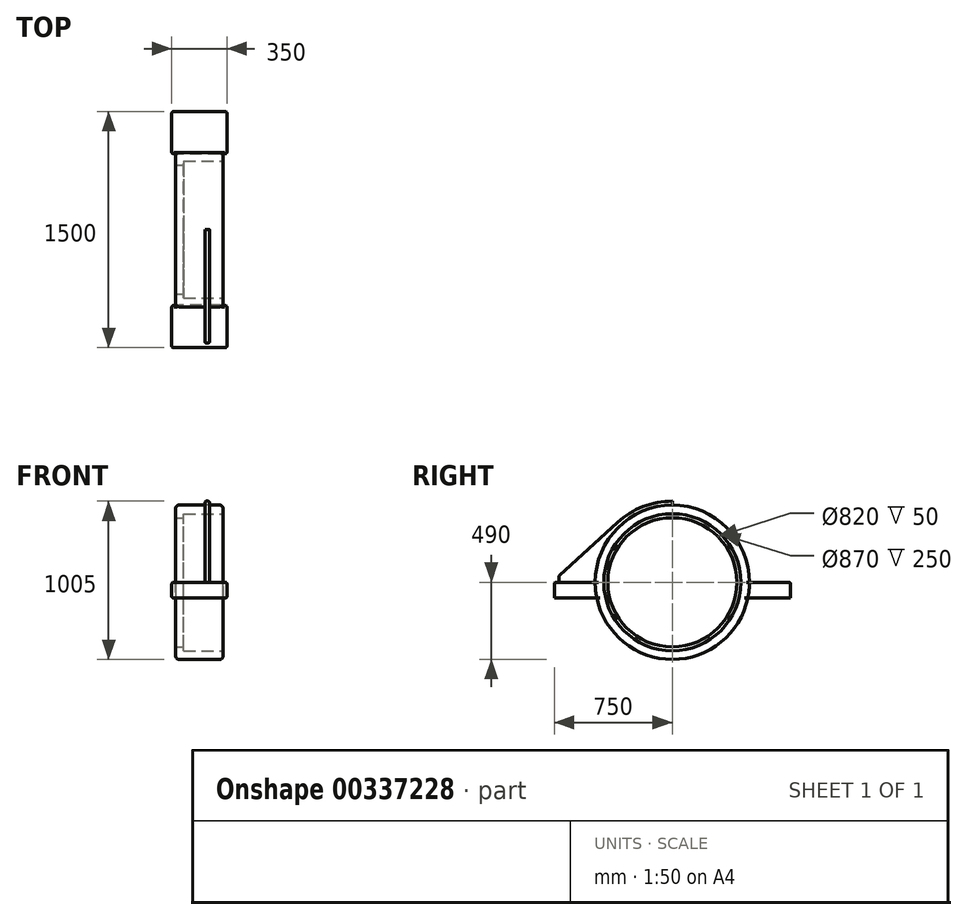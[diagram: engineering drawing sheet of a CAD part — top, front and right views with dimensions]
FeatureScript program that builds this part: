
annotation { "Feature Type Name" : "Feature", "Feature Type Description" : "" }
export const myFeature = defineFeature(function(context is Context, id is Id, definition is map)
    precondition{}
    {
        {
            var Q0;
            Q0=qCreatedBy(makeId("Front.planeOp"),FACE);
            var sketch = newSketch(context, id + "F0", { "sketchPlane" : qUnion([Q0])});
            skLineSegment(sketch, "E0", {"start": v(150, 435) * mm, "end": v(150, 490) * mm});
            skLineSegment(sketch, "E1", {"start": v(150, 490) * mm, "end": v(-150, 490) * mm});
            skLineSegment(sketch, "E2", {"start": v(-150, 490) * mm, "end": v(-150, 410) * mm});
            skLineSegment(sketch, "E3", {"start": v(0, 490) * mm, "end": v(0, 0) * mm, "construction": true});
            skLineSegment(sketch, "E4", {"start": v(0, 0) * mm, "end": v(-175, 0) * mm, "construction": true});
            skLineSegment(sketch, "E5", {"start": v(-100, 435) * mm, "end": v(-100, 410) * mm});
            skLineSegment(sketch, "E6", {"start": v(-100, 410) * mm, "end": v(-150, 410) * mm});
            skLineSegment(sketch, "E7", {"start": v(-100, 435) * mm, "end": v(150, 435) * mm});
            skSolve(sketch);
        }
        {
            var Q0;
            Q0=qSketchRegion(id+"F0",true);
            var Q1;
            Q1=sQuery(id+"F0.wireOp",EDGE,"E4");
            revolve(context, id + "F1", {"entities" : qUnion([Q0]), "axis" : qUnion([Q1]), "revolveType" : RevolveType.FULL});
        }
        {
            var Q0;
            Q0=qCreatedBy(makeId("Right.planeOp"),FACE);
            var sketch = newSketch(context, id + "F2", { "sketchPlane" : qUnion([Q0])});
            skLineSegment(sketch, "E8.bottom", {"start": v(-750, 0) * mm, "end": v(750, 0) * mm});
            skLineSegment(sketch, "E8.top", {"start": v(-750, -100) * mm, "end": v(750, -100) * mm});
            skLineSegment(sketch, "E8.left", {"start": v(-750, 0) * mm, "end": v(-750, -100) * mm});
            skLineSegment(sketch, "E8.right", {"start": v(750, 0) * mm, "end": v(750, -100) * mm});
            skLineSegment(sketch, "E9", {"start": v(-750, -50) * mm, "end": v(750, -50) * mm, "construction": true});
            skLineSegment(sketch, "E10", {"start": v(0, 0) * mm, "end": v(0, -50) * mm});
            skCircle(sketch, "E11.0", {"center": v(0, 0) * mm, "radius": 490 * mm});
            skSolve(sketch);
        }
        {
            var Q0;
            {var subQ0=sQuery(id+"F2.wireOp",EDGE,"E8.left");Q0=makeQuery(id+"F2.imprint","IMPRINT",FACE,{"disambiguationData":[TD([[makeQuery(id+"F2.imprint","IMPRINT",EDGE,{"derivedFrom":subQ0}),1.0]])]});}
            var Q1;
            {var subQ0=sQuery(id+"F2.wireOp",EDGE,"E8.right");Q1=makeQuery(id+"F2.imprint","IMPRINT",FACE,{"disambiguationData":[TD([[makeQuery(id+"F2.imprint","IMPRINT",EDGE,{"derivedFrom":subQ0}),-1.0]])]});}
            extrude(context, id + "F3", {"entities" : qUnion([Q0, Q1]), "operationType" : NewBodyOperationType.ADD, "depth" : 350 * mm, "symmetric" : true});
        }
        {
            var Q0;
            Q0=qCreatedBy(makeId("Right.planeOp"),FACE);
            cPlane(context, id + "F4", {"entities" : qUnion([Q0]), "cplaneType" : CPlaneType.OFFSET, "offset" : 50 * mm, "width" : 150 * mm, "height" : 150 * mm});
        }
        {
            var Q0;
            Q0=qCreatedBy(id+"F4.planeOp",FACE);
            var sketch = newSketch(context, id + "F5", { "sketchPlane" : qUnion([Q0])});
            skLineSegment(sketch, "E12", {"start": v(0, 0) * mm, "end": v(0, 515) * mm});
            skLineSegment(sketch, "E13", {"start": v(-720, 0) * mm, "end": v(-720, 40) * mm});
            skLineSegment(sketch, "E14", {"start": v(-720, 40) * mm, "end": v(-347.24, 380.33) * mm});
            skArc(sketch, "E15", {"start": v(0, 515) * mm, "mid": v(-186.22, 480.15) * mm, "end": v(-347.24, 380.33) * mm});
            skLineSegment(sketch, "E16.0", {"start": v(-720, 0) * mm, "end": v(-490, 0) * mm});
            skPoint(sketch, "E17.orphan", {"position": v(-750, 0) * mm});
            skLineSegment(sketch, "E18", {"start": v(-490, 0) * mm, "end": v(0, 0) * mm});
            skArc(sketch, "E19.0", {"start": v(0, 490) * mm, "mid": v(-346.48, 346.48) * mm, "end": v(-490, 0) * mm});
            skPoint(sketch, "E20.orphan", {"position": v(490, 0) * mm});
            skSolve(sketch);
        }
        {
            var Q0;
            Q0=makeQuery(id+"F5.imprint","IMPRINT",FACE,{"disambiguationData":[TD([[makeQuery(id+"F5.imprint","IMPRINT",EDGE,{"derivedFrom":sQuery(id+"F5.wireOp",EDGE,"E13")}),-1.0]])]});
            extrude(context, id + "F6", {"entities" : qUnion([Q0]), "operationType" : NewBodyOperationType.ADD, "depth" : 30 * mm, "symmetric" : true});
        }
        {
            var Q0;
            Q0=makeQuery(id+"F6.opExtrude","CAP_EDGE",EDGE,{"disambiguationData":[OSD([sQuery(id+"F5.wireOp",EDGE,"E16.0")])],"isStart":false});
            var Q1;
            Q1=makeQuery(id+"F6.opExtrude","SWEPT_EDGE",EDGE,{"disambiguationData":[OSD([sQuery(id+"F5.wireOp",EDGE,"E13"),sQuery(id+"F5.wireOp",EDGE,"E16.0")])]});
            var Q2;
            Q2=makeQuery(id+"F6.opExtrude","CAP_EDGE",EDGE,{"disambiguationData":[OSD([sQuery(id+"F5.wireOp",EDGE,"E13")])],"isStart":false});
            var Q3;
            Q3=makeQuery(id+"F6.opExtrude","CAP_EDGE",EDGE,{"disambiguationData":[OSD([sQuery(id+"F5.wireOp",EDGE,"E14")])],"isStart":false});
            var Q4;
            Q4=makeQuery(id+"F6.opExtrude","SWEPT_EDGE",EDGE,{"disambiguationData":[OSD([sQuery(id+"F5.wireOp",EDGE,"E13"),sQuery(id+"F5.wireOp",EDGE,"E14")])]});
            var Q5;
            Q5=makeQuery(id+"F6.opExtrude","CAP_EDGE",EDGE,{"disambiguationData":[OSD([sQuery(id+"F5.wireOp",EDGE,"E14")])],"isStart":true});
            var Q6;
            Q6=makeQuery(id+"F6.opExtrude","CAP_EDGE",EDGE,{"disambiguationData":[OSD([sQuery(id+"F5.wireOp",EDGE,"E13")])],"isStart":true});
            var Q7;
            {var subQ0=sQuery(id+"F5.wireOp",EDGE,"E19.0");Q7=makeQuery(id+"F4xZpk5MUKX7Juj_1.1.F6.boolean.opBoolean","MERGE",EDGE,{"derivedFrom":[makeQuery(id+"F6.opExtrude","CAP_EDGE",EDGE,{"disambiguationData":[OSD([subQ0])],"isStart":true}),makeQuery(id+"F4xZpk5MUKX7Juj_1.1.F6.opExtrude","CAP_EDGE",EDGE,{"disambiguationData":[OSD([subQ0])],"isStart":true})]});}
            var Q8;
            {var subQ0=makeQuery(id+"F1.opRevolve","SWEPT_FACE",FACE,{"disambiguationData":[OSD([sQuery(id+"F0.wireOp",EDGE,"E1")])]});var subQ1=sQuery(id+"F5.wireOp",EDGE,"E19.0");var subQ2=sQuery(id+"F5.wireOp",EDGE,"E16.0");var subQ3=sQuery(id+"F5.wireOp",EDGE,"E15");var subQ4=sQuery(id+"F5.wireOp",EDGE,"E14");var subQ5=sQuery(id+"F5.wireOp",EDGE,"E13");var subQ6=sQuery(id+"F5.wireOp",EDGE,"E12");var subQ7=sQuery(id+"F2.wireOp",EDGE,"E8.bottom");var subQ8=sQuery(id+"F2.wireOp",EDGE,"E11.0");var subQ9=makeQuery(id+"F2.imprint","INTERSECT",VERTEX,{"disambiguationData":[OD(0.0)],"derivedFrom":[subQ7,subQ8]});var subQ10=makeQuery(id+"F3.opExtrude","SWEPT_FACE",FACE,{"disambiguationData":[OSD([subQ7]),TDD([makeQuery(id+"F2.imprint","IMPRINT",EDGE,{"disambiguationData":[TD([[makeQuery(id+"F2.imprint","INTERSECT",VERTEX,{"derivedFrom":[subQ7,sQuery(id+"F2.wireOp",EDGE,"E8.left")]}),-1.0]])],"derivedFrom":subQ7})])]});var subQ11=makeQuery(id+"F6.opExtrude","CAP_FACE",FACE,{"disambiguationData":[OSD([subQ6,subQ5,subQ4,subQ3,subQ2,subQ1])],"isStart":true});Q8=makeQuery(id+"FQAO3xyy8PO0jJj_1.1.F6.boolean.opBoolean","SPLIT",EDGE,{"disambiguationData":[TD([subQ11])],"derivedFrom":makeQuery(id+"F6.boolean.opBoolean","SPLIT",EDGE,{"disambiguationData":[TD([makeQuery(id+"F1.opRevolve","SWEPT_FACE",FACE,{"disambiguationData":[OSD([sQuery(id+"F0.wireOp",EDGE,"E2")])]})])],"derivedFrom":makeQuery(id+"F3.boolean.opBoolean","SPLIT",EDGE,{"disambiguationData":[topologyDisambiguationEdgeConnected([subQ0,subQ10])],"derivedFrom":makeQuery(id+"F3.opExtrude","SWEPT_EDGE",EDGE,{"disambiguationData":[OSD([subQ7,subQ8]),TDD([subQ9])]})})})});}
            var Q9;
            {var subQ0=sQuery(id+"F5.wireOp",EDGE,"E19.0");Q9=makeQuery(id+"F4xZpk5MUKX7Juj_1.1.FQAO3xyy8PO0jJj_1.1.F6.boolean.opBoolean","MERGE",EDGE,{"derivedFrom":[makeQuery(id+"FQAO3xyy8PO0jJj_1.1.F6.opExtrude","CAP_EDGE",EDGE,{"disambiguationData":[OSD([subQ0])],"isStart":true}),makeQuery(id+"F4xZpk5MUKX7Juj_1.1.FQAO3xyy8PO0jJj_1.1.F6.opExtrude","CAP_EDGE",EDGE,{"disambiguationData":[OSD([subQ0])],"isStart":true})]});}
            var Q10;
            Q10=makeQuery(id+"FQAO3xyy8PO0jJj_1.1.F6.opExtrude","CAP_EDGE",EDGE,{"disambiguationData":[OSD([sQuery(id+"F5.wireOp",EDGE,"E16.0")])],"isStart":true});
            var Q11;
            Q11=makeQuery(id+"FQAO3xyy8PO0jJj_1.1.F6.opExtrude","CAP_EDGE",EDGE,{"disambiguationData":[OSD([sQuery(id+"F5.wireOp",EDGE,"E14")])],"isStart":true});
            var Q12;
            Q12=makeQuery(id+"FQAO3xyy8PO0jJj_1.1.F6.opExtrude","CAP_EDGE",EDGE,{"disambiguationData":[OSD([sQuery(id+"F5.wireOp",EDGE,"E14")])],"isStart":false});
            var Q13;
            {var subQ0=sQuery(id+"F5.wireOp",EDGE,"E19.0");Q13=makeQuery(id+"F4xZpk5MUKX7Juj_1.1.F6.boolean.opBoolean","MERGE",EDGE,{"derivedFrom":[makeQuery(id+"F6.opExtrude","CAP_EDGE",EDGE,{"disambiguationData":[OSD([subQ0])],"isStart":false}),makeQuery(id+"F4xZpk5MUKX7Juj_1.1.F6.opExtrude","CAP_EDGE",EDGE,{"disambiguationData":[OSD([subQ0])],"isStart":false})]});}
            var Q14;
            {var subQ0=sQuery(id+"F5.wireOp",EDGE,"E19.0");Q14=makeQuery(id+"F4xZpk5MUKX7Juj_1.1.FQAO3xyy8PO0jJj_1.1.F6.boolean.opBoolean","MERGE",EDGE,{"derivedFrom":[makeQuery(id+"FQAO3xyy8PO0jJj_1.1.F6.opExtrude","CAP_EDGE",EDGE,{"disambiguationData":[OSD([subQ0])],"isStart":false}),makeQuery(id+"F4xZpk5MUKX7Juj_1.1.FQAO3xyy8PO0jJj_1.1.F6.opExtrude","CAP_EDGE",EDGE,{"disambiguationData":[OSD([subQ0])],"isStart":false})]});}
            var Q15;
            {var subQ0=sQuery(id+"F2.wireOp",EDGE,"E11.0");var subQ1=sQuery(id+"F2.wireOp",EDGE,"E8.bottom");var subQ2=makeQuery(id+"F2.imprint","INTERSECT",VERTEX,{"disambiguationData":[OD(0.0)],"derivedFrom":[subQ1,subQ0]});var subQ4=makeQuery(id+"F3.opExtrude","SWEPT_FACE",FACE,{"disambiguationData":[OSD([subQ1]),TDD([makeQuery(id+"F2.imprint","IMPRINT",EDGE,{"disambiguationData":[TD([[makeQuery(id+"F2.imprint","INTERSECT",VERTEX,{"derivedFrom":[subQ1,sQuery(id+"F2.wireOp",EDGE,"E8.left")]}),-1.0]])],"derivedFrom":subQ1})])]});var subQ5=makeQuery(id+"F1.opRevolve","SWEPT_FACE",FACE,{"disambiguationData":[OSD([sQuery(id+"F0.wireOp",EDGE,"E1")])]});var subQ6=makeQuery(id+"F1.opRevolve","SWEPT_FACE",FACE,{"disambiguationData":[OSD([sQuery(id+"F0.wireOp",EDGE,"E2")])]});Q15=makeQuery(id+"FQAO3xyy8PO0jJj_1.1.F6.boolean.opBoolean","SPLIT",EDGE,{"disambiguationData":[TD([subQ6])],"derivedFrom":makeQuery(id+"F6.boolean.opBoolean","SPLIT",EDGE,{"disambiguationData":[TD([subQ6])],"derivedFrom":makeQuery(id+"F3.boolean.opBoolean","SPLIT",EDGE,{"disambiguationData":[topologyDisambiguationEdgeConnected([subQ5,subQ4])],"derivedFrom":makeQuery(id+"F3.opExtrude","SWEPT_EDGE",EDGE,{"disambiguationData":[OSD([subQ1,subQ0]),TDD([subQ2])]})})})});}
            var Q16;
            Q16=makeQuery(id+"FQAO3xyy8PO0jJj_1.1.F6.opExtrude","CAP_EDGE",EDGE,{"disambiguationData":[OSD([sQuery(id+"F5.wireOp",EDGE,"E16.0")])],"isStart":false});
            var Q17;
            Q17=makeQuery(id+"FQAO3xyy8PO0jJj_1.1.F6.opExtrude","SWEPT_EDGE",EDGE,{"disambiguationData":[OSD([sQuery(id+"F5.wireOp",EDGE,"E13"),sQuery(id+"F5.wireOp",EDGE,"E16.0")])]});
            var Q18;
            {var subQ0=sQuery(id+"F2.wireOp",EDGE,"E11.0");var subQ1=sQuery(id+"F2.wireOp",EDGE,"E8.bottom");var subQ2=makeQuery(id+"F2.imprint","INTERSECT",VERTEX,{"disambiguationData":[OD(0.0)],"derivedFrom":[subQ1,subQ0]});var subQ3=makeQuery(id+"F3.opExtrude","SWEPT_FACE",FACE,{"disambiguationData":[OSD([subQ1]),TDD([makeQuery(id+"F2.imprint","IMPRINT",EDGE,{"disambiguationData":[TD([[makeQuery(id+"F2.imprint","INTERSECT",VERTEX,{"derivedFrom":[subQ1,sQuery(id+"F2.wireOp",EDGE,"E8.left")]}),-1.0]])],"derivedFrom":subQ1})])]});var subQ4=makeQuery(id+"F1.opRevolve","SWEPT_FACE",FACE,{"disambiguationData":[OSD([sQuery(id+"F0.wireOp",EDGE,"E1")])]});Q18=makeQuery(id+"F6.boolean.opBoolean","SPLIT",EDGE,{"disambiguationData":[TD([makeQuery(id+"F1.opRevolve","SWEPT_FACE",FACE,{"disambiguationData":[OSD([sQuery(id+"F0.wireOp",EDGE,"E0")])]})])],"derivedFrom":makeQuery(id+"F3.boolean.opBoolean","SPLIT",EDGE,{"disambiguationData":[topologyDisambiguationEdgeConnected([subQ4,subQ3])],"derivedFrom":makeQuery(id+"F3.opExtrude","SWEPT_EDGE",EDGE,{"disambiguationData":[OSD([subQ1,subQ0]),TDD([subQ2])]})})});}
            var Q19;
            Q19=makeQuery(id+"F4xZpk5MUKX7Juj_1.1.FQAO3xyy8PO0jJj_1.1.F6.opExtrude","SWEPT_EDGE",EDGE,{"disambiguationData":[OSD([sQuery(id+"F5.wireOp",EDGE,"E13"),sQuery(id+"F5.wireOp",EDGE,"E14")])]});
            var Q20;
            Q20=makeQuery(id+"F4xZpk5MUKX7Juj_1.1.F6.opExtrude","SWEPT_EDGE",EDGE,{"disambiguationData":[OSD([sQuery(id+"F5.wireOp",EDGE,"E13"),sQuery(id+"F5.wireOp",EDGE,"E14")])]});
            var Q21;
            Q21=makeQuery(id+"F4xZpk5MUKX7Juj_1.1.F6.opExtrude","CAP_EDGE",EDGE,{"disambiguationData":[OSD([sQuery(id+"F5.wireOp",EDGE,"E13")])],"isStart":true});
            var Q22;
            Q22=makeQuery(id+"F4xZpk5MUKX7Juj_1.1.F6.opExtrude","CAP_EDGE",EDGE,{"disambiguationData":[OSD([sQuery(id+"F5.wireOp",EDGE,"E13")])],"isStart":false});
            var Q23;
            Q23=makeQuery(id+"F4xZpk5MUKX7Juj_1.1.F6.opExtrude","SWEPT_EDGE",EDGE,{"disambiguationData":[OSD([sQuery(id+"F5.wireOp",EDGE,"E13"),sQuery(id+"F5.wireOp",EDGE,"E16.0")])]});
            var Q24;
            Q24=makeQuery(id+"F4xZpk5MUKX7Juj_1.1.FQAO3xyy8PO0jJj_1.1.F6.opExtrude","SWEPT_EDGE",EDGE,{"disambiguationData":[OSD([sQuery(id+"F5.wireOp",EDGE,"E13"),sQuery(id+"F5.wireOp",EDGE,"E16.0")])]});
            var Q25;
            Q25=makeQuery(id+"F4xZpk5MUKX7Juj_1.1.FQAO3xyy8PO0jJj_1.1.F6.opExtrude","CAP_EDGE",EDGE,{"disambiguationData":[OSD([sQuery(id+"F5.wireOp",EDGE,"E13")])],"isStart":false});
            var Q26;
            {var subQ0=sQuery(id+"F5.wireOp",EDGE,"E19.0");var subQ1=sQuery(id+"F5.wireOp",EDGE,"E16.0");var subQ2=sQuery(id+"F5.wireOp",EDGE,"E15");var subQ3=sQuery(id+"F5.wireOp",EDGE,"E14");var subQ4=sQuery(id+"F5.wireOp",EDGE,"E13");var subQ5=sQuery(id+"F5.wireOp",EDGE,"E12");var subQ6=makeQuery(id+"F6.opExtrude","CAP_FACE",FACE,{"disambiguationData":[OSD([subQ5,subQ4,subQ3,subQ2,subQ1,subQ0])],"isStart":true});var subQ7=sQuery(id+"F2.wireOp",EDGE,"E8.bottom");var subQ8=sQuery(id+"F2.wireOp",EDGE,"E11.0");var subQ9=makeQuery(id+"F2.imprint","INTERSECT",VERTEX,{"disambiguationData":[OD(1.0)],"derivedFrom":[subQ7,subQ8]});var subQ10=makeQuery(id+"F3.opExtrude","SWEPT_FACE",FACE,{"disambiguationData":[OSD([subQ7]),TDD([makeQuery(id+"F2.imprint","IMPRINT",EDGE,{"disambiguationData":[TD([[makeQuery(id+"F2.imprint","INTERSECT",VERTEX,{"derivedFrom":[subQ7,sQuery(id+"F2.wireOp",EDGE,"E8.right")]}),1.0]])],"derivedFrom":subQ7})])]});var subQ11=makeQuery(id+"F1.opRevolve","SWEPT_FACE",FACE,{"disambiguationData":[OSD([sQuery(id+"F0.wireOp",EDGE,"E1")])]});Q26=makeQuery(id+"F4xZpk5MUKX7Juj_1.1.FQAO3xyy8PO0jJj_1.1.F6.boolean.opBoolean","SPLIT",EDGE,{"disambiguationData":[TD([subQ6])],"derivedFrom":makeQuery(id+"F4xZpk5MUKX7Juj_1.1.F6.boolean.opBoolean","SPLIT",EDGE,{"disambiguationData":[TD([makeQuery(id+"F1.opRevolve","SWEPT_FACE",FACE,{"disambiguationData":[OSD([sQuery(id+"F0.wireOp",EDGE,"E2")])]})])],"derivedFrom":makeQuery(id+"F3.boolean.opBoolean","SPLIT",EDGE,{"disambiguationData":[topologyDisambiguationEdgeConnected([subQ11,subQ10])],"derivedFrom":makeQuery(id+"F3.opExtrude","SWEPT_EDGE",EDGE,{"disambiguationData":[OSD([subQ7,subQ8]),TDD([subQ9])]})})})});}
            var Q27;
            {var subQ0=sQuery(id+"F2.wireOp",EDGE,"E11.0");var subQ1=sQuery(id+"F2.wireOp",EDGE,"E8.bottom");var subQ2=makeQuery(id+"F2.imprint","INTERSECT",VERTEX,{"disambiguationData":[OD(1.0)],"derivedFrom":[subQ1,subQ0]});var subQ4=makeQuery(id+"F1.opRevolve","SWEPT_FACE",FACE,{"disambiguationData":[OSD([sQuery(id+"F0.wireOp",EDGE,"E1")])]});var subQ5=makeQuery(id+"F1.opRevolve","SWEPT_FACE",FACE,{"disambiguationData":[OSD([sQuery(id+"F0.wireOp",EDGE,"E2")])]});var subQ6=makeQuery(id+"F3.opExtrude","SWEPT_FACE",FACE,{"disambiguationData":[OSD([subQ1]),TDD([makeQuery(id+"F2.imprint","IMPRINT",EDGE,{"disambiguationData":[TD([[makeQuery(id+"F2.imprint","INTERSECT",VERTEX,{"derivedFrom":[subQ1,sQuery(id+"F2.wireOp",EDGE,"E8.right")]}),1.0]])],"derivedFrom":subQ1})])]});Q27=makeQuery(id+"F4xZpk5MUKX7Juj_1.1.FQAO3xyy8PO0jJj_1.1.F6.boolean.opBoolean","SPLIT",EDGE,{"disambiguationData":[TD([subQ5])],"derivedFrom":makeQuery(id+"F4xZpk5MUKX7Juj_1.1.F6.boolean.opBoolean","SPLIT",EDGE,{"disambiguationData":[TD([subQ5])],"derivedFrom":makeQuery(id+"F3.boolean.opBoolean","SPLIT",EDGE,{"disambiguationData":[topologyDisambiguationEdgeConnected([subQ4,subQ6])],"derivedFrom":makeQuery(id+"F3.opExtrude","SWEPT_EDGE",EDGE,{"disambiguationData":[OSD([subQ1,subQ0]),TDD([subQ2])]})})})});}
            var Q28;
            {var subQ0=sQuery(id+"F2.wireOp",EDGE,"E11.0");var subQ1=sQuery(id+"F2.wireOp",EDGE,"E8.bottom");var subQ2=makeQuery(id+"F2.imprint","INTERSECT",VERTEX,{"disambiguationData":[OD(1.0)],"derivedFrom":[subQ1,subQ0]});var subQ3=makeQuery(id+"F1.opRevolve","SWEPT_FACE",FACE,{"disambiguationData":[OSD([sQuery(id+"F0.wireOp",EDGE,"E1")])]});var subQ10=makeQuery(id+"F3.opExtrude","SWEPT_FACE",FACE,{"disambiguationData":[OSD([subQ1]),TDD([makeQuery(id+"F2.imprint","IMPRINT",EDGE,{"disambiguationData":[TD([[makeQuery(id+"F2.imprint","INTERSECT",VERTEX,{"derivedFrom":[subQ1,sQuery(id+"F2.wireOp",EDGE,"E8.right")]}),1.0]])],"derivedFrom":subQ1})])]});Q28=makeQuery(id+"F4xZpk5MUKX7Juj_1.1.F6.boolean.opBoolean","SPLIT",EDGE,{"disambiguationData":[TD([makeQuery(id+"F1.opRevolve","SWEPT_FACE",FACE,{"disambiguationData":[OSD([sQuery(id+"F0.wireOp",EDGE,"E0")])]})])],"derivedFrom":makeQuery(id+"F3.boolean.opBoolean","SPLIT",EDGE,{"disambiguationData":[topologyDisambiguationEdgeConnected([subQ3,subQ10])],"derivedFrom":makeQuery(id+"F3.opExtrude","SWEPT_EDGE",EDGE,{"disambiguationData":[OSD([subQ1,subQ0]),TDD([subQ2])]})})});}
            var Q29;
            {var subQ0=sQuery(id+"F2.wireOp",EDGE,"E8.top");var subQ1=sQuery(id+"F2.wireOp",EDGE,"E11.0");var subQ2=makeQuery(id+"F2.imprint","INTERSECT",VERTEX,{"disambiguationData":[OD(1.0)],"derivedFrom":[subQ0,subQ1]});Q29=makeQuery(id+"F3.boolean.opBoolean","SPLIT",EDGE,{"disambiguationData":[topologyDisambiguationEdgeConnected([makeQuery(id+"F1.opRevolve","SWEPT_FACE",FACE,{"disambiguationData":[OSD([sQuery(id+"F0.wireOp",EDGE,"E1")])]}),makeQuery(id+"F3.opExtrude","SWEPT_FACE",FACE,{"disambiguationData":[OSD([subQ0]),TDD([makeQuery(id+"F2.imprint","IMPRINT",EDGE,{"disambiguationData":[TD([[makeQuery(id+"F2.imprint","INTERSECT",VERTEX,{"derivedFrom":[subQ0,sQuery(id+"F2.wireOp",EDGE,"E8.right")]}),1.0]])],"derivedFrom":subQ0})])]})])],"derivedFrom":makeQuery(id+"F3.opExtrude","SWEPT_EDGE",EDGE,{"disambiguationData":[OSD([subQ0,subQ1]),TDD([subQ2])]})});}
            var Q30;
            {var subQ0=sQuery(id+"F2.wireOp",EDGE,"E8.top");var subQ1=sQuery(id+"F2.wireOp",EDGE,"E11.0");var subQ2=makeQuery(id+"F2.imprint","INTERSECT",VERTEX,{"disambiguationData":[OD(0.0)],"derivedFrom":[subQ0,subQ1]});Q30=makeQuery(id+"F3.boolean.opBoolean","SPLIT",EDGE,{"disambiguationData":[topologyDisambiguationEdgeConnected([makeQuery(id+"F1.opRevolve","SWEPT_FACE",FACE,{"disambiguationData":[OSD([sQuery(id+"F0.wireOp",EDGE,"E1")])]}),makeQuery(id+"F3.opExtrude","SWEPT_FACE",FACE,{"disambiguationData":[OSD([subQ0]),TDD([makeQuery(id+"F2.imprint","IMPRINT",EDGE,{"disambiguationData":[TD([[makeQuery(id+"F2.imprint","INTERSECT",VERTEX,{"derivedFrom":[subQ0,sQuery(id+"F2.wireOp",EDGE,"E8.left")]}),-1.0]])],"derivedFrom":subQ0})])]})])],"derivedFrom":makeQuery(id+"F3.opExtrude","SWEPT_EDGE",EDGE,{"disambiguationData":[OSD([subQ0,subQ1]),TDD([subQ2])]})});}
            var Q31;
            Q31=makeQuery(id+"FQAO3xyy8PO0jJj_1.1.F6.opExtrude","CAP_EDGE",EDGE,{"disambiguationData":[OSD([sQuery(id+"F5.wireOp",EDGE,"E13")])],"isStart":true});
            var Q32;
            Q32=makeQuery(id+"FQAO3xyy8PO0jJj_1.1.F6.opExtrude","CAP_EDGE",EDGE,{"disambiguationData":[OSD([sQuery(id+"F5.wireOp",EDGE,"E13")])],"isStart":false});
            var Q33;
            Q33=makeQuery(id+"F4xZpk5MUKX7Juj_1.1.FQAO3xyy8PO0jJj_1.1.F6.opExtrude","CAP_EDGE",EDGE,{"disambiguationData":[OSD([sQuery(id+"F5.wireOp",EDGE,"E13")])],"isStart":true});
            fillet(context, id + "F7", {"entities" : qUnion([Q0, Q1, Q2, Q3, Q4, Q5, Q6, Q7, Q8, Q9, Q10, Q11, Q12, Q13, Q14, Q15, Q16, Q17, Q18, Q19, Q20, Q21, Q22, Q23, Q24, Q25, Q26, Q27, Q28, Q29, Q30, Q31, Q32, Q33]), "radius" : 10 * mm, "tangentPropagation" : true, "allowEdgeOverflow" : false});
        }
        {
            var Q0;
            {var subQ0=sQuery(id+"F0.wireOp",EDGE,"E2");var subQ1=sQuery(id+"F2.wireOp",EDGE,"E11.0");Q0=makeQuery(id+"F3.boolean.opBoolean","SPLIT",EDGE,{"disambiguationData":[topologyDisambiguationEdgeConnected([makeQuery(id+"F1.opRevolve","SWEPT_FACE",FACE,{"disambiguationData":[OSD([subQ0])]}),makeQuery(id+"F3.opExtrude","SWEPT_FACE",FACE,{"disambiguationData":[OSD([subQ1]),TDD([makeQuery(id+"F2.imprint","IMPRINT",EDGE,{"disambiguationData":[TD([[makeQuery(id+"F2.imprint","INTERSECT",VERTEX,{"disambiguationData":[OD(1.0)],"derivedFrom":[sQuery(id+"F2.wireOp",EDGE,"E8.bottom"),subQ1]}),1.0]])],"derivedFrom":subQ1})])]})])],"derivedFrom":makeQuery(id+"F1.opRevolve","SWEPT_EDGE",EDGE,{"disambiguationData":[OSD([sQuery(id+"F0.wireOp",EDGE,"E1"),subQ0])]})});}
            var Q1;
            {var subQ0=sQuery(id+"F0.wireOp",EDGE,"E2");var subQ1=sQuery(id+"F2.wireOp",EDGE,"E11.0");Q1=makeQuery(id+"F3.boolean.opBoolean","SPLIT",EDGE,{"disambiguationData":[topologyDisambiguationEdgeConnected([makeQuery(id+"F1.opRevolve","SWEPT_FACE",FACE,{"disambiguationData":[OSD([subQ0])]}),makeQuery(id+"F3.opExtrude","SWEPT_FACE",FACE,{"disambiguationData":[OSD([subQ1]),TDD([makeQuery(id+"F2.imprint","IMPRINT",EDGE,{"disambiguationData":[TD([[makeQuery(id+"F2.imprint","INTERSECT",VERTEX,{"disambiguationData":[OD(0.0)],"derivedFrom":[sQuery(id+"F2.wireOp",EDGE,"E8.bottom"),subQ1]}),-1.0]])],"derivedFrom":subQ1})])]})])],"derivedFrom":makeQuery(id+"F1.opRevolve","SWEPT_EDGE",EDGE,{"disambiguationData":[OSD([sQuery(id+"F0.wireOp",EDGE,"E1"),subQ0])]})});}
            var Q2;
            {var subQ0=sQuery(id+"F0.wireOp",EDGE,"E0");var subQ1=sQuery(id+"F2.wireOp",EDGE,"E11.0");Q2=makeQuery(id+"F3.boolean.opBoolean","SPLIT",EDGE,{"disambiguationData":[topologyDisambiguationEdgeConnected([makeQuery(id+"F1.opRevolve","SWEPT_FACE",FACE,{"disambiguationData":[OSD([subQ0])]}),makeQuery(id+"F3.opExtrude","SWEPT_FACE",FACE,{"disambiguationData":[OSD([subQ1]),TDD([makeQuery(id+"F2.imprint","IMPRINT",EDGE,{"disambiguationData":[TD([[makeQuery(id+"F2.imprint","INTERSECT",VERTEX,{"disambiguationData":[OD(0.0)],"derivedFrom":[sQuery(id+"F2.wireOp",EDGE,"E8.bottom"),subQ1]}),-1.0]])],"derivedFrom":subQ1})])]})])],"derivedFrom":makeQuery(id+"F1.opRevolve","SWEPT_EDGE",EDGE,{"disambiguationData":[OSD([subQ0,sQuery(id+"F0.wireOp",EDGE,"E1")])]})});}
            var Q3;
            {var subQ0=sQuery(id+"F0.wireOp",EDGE,"E0");var subQ1=sQuery(id+"F2.wireOp",EDGE,"E11.0");Q3=makeQuery(id+"F3.boolean.opBoolean","SPLIT",EDGE,{"disambiguationData":[topologyDisambiguationEdgeConnected([makeQuery(id+"F1.opRevolve","SWEPT_FACE",FACE,{"disambiguationData":[OSD([subQ0])]}),makeQuery(id+"F3.opExtrude","SWEPT_FACE",FACE,{"disambiguationData":[OSD([subQ1]),TDD([makeQuery(id+"F2.imprint","IMPRINT",EDGE,{"disambiguationData":[TD([[makeQuery(id+"F2.imprint","INTERSECT",VERTEX,{"disambiguationData":[OD(1.0)],"derivedFrom":[sQuery(id+"F2.wireOp",EDGE,"E8.bottom"),subQ1]}),1.0]])],"derivedFrom":subQ1})])]})])],"derivedFrom":makeQuery(id+"F1.opRevolve","SWEPT_EDGE",EDGE,{"disambiguationData":[OSD([subQ0,sQuery(id+"F0.wireOp",EDGE,"E1")])]})});}
            fillet(context, id + "F8", {"entities" : qUnion([Q0, Q1, Q2, Q3]), "radius" : 20 * mm, "tangentPropagation" : true, "allowEdgeOverflow" : false});
        }
        {
            var Q0;
            {var subQ0=sQuery(id+"F2.wireOp",EDGE,"E8.bottom");Q0=makeQuery(id+"F3.opExtrude","CAP_EDGE",EDGE,{"disambiguationData":[OSD([subQ0]),TDD([makeQuery(id+"F2.imprint","IMPRINT",EDGE,{"disambiguationData":[TD([[makeQuery(id+"F2.imprint","INTERSECT",VERTEX,{"derivedFrom":[subQ0,sQuery(id+"F2.wireOp",EDGE,"E8.right")]}),1.0]])],"derivedFrom":subQ0})])],"isStart":false});}
            var Q1;
            Q1=makeQuery(id+"F3.opExtrude","CAP_EDGE",EDGE,{"disambiguationData":[OSD([sQuery(id+"F2.wireOp",EDGE,"E8.right")])],"isStart":false});
            var Q2;
            {var subQ0=sQuery(id+"F2.wireOp",EDGE,"E11.0");Q2=makeQuery(id+"F3.opExtrude","CAP_EDGE",EDGE,{"disambiguationData":[OSD([subQ0]),TDD([makeQuery(id+"F2.imprint","IMPRINT",EDGE,{"disambiguationData":[TD([[makeQuery(id+"F2.imprint","INTERSECT",VERTEX,{"disambiguationData":[OD(1.0)],"derivedFrom":[sQuery(id+"F2.wireOp",EDGE,"E8.bottom"),subQ0]}),1.0]])],"derivedFrom":subQ0})])],"isStart":false});}
            var Q3;
            Q3=makeQuery(id+"F3.opExtrude","SWEPT_EDGE",EDGE,{"disambiguationData":[OSD([sQuery(id+"F2.wireOp",EDGE,"E8.bottom"),sQuery(id+"F2.wireOp",EDGE,"E8.right")])]});
            var Q4;
            Q4=makeQuery(id+"F3.opExtrude","CAP_EDGE",EDGE,{"disambiguationData":[OSD([sQuery(id+"F2.wireOp",EDGE,"E8.right")])],"isStart":true});
            var Q5;
            {var subQ0=sQuery(id+"F2.wireOp",EDGE,"E8.bottom");Q5=makeQuery(id+"F3.opExtrude","CAP_EDGE",EDGE,{"disambiguationData":[OSD([subQ0]),TDD([makeQuery(id+"F2.imprint","IMPRINT",EDGE,{"disambiguationData":[TD([[makeQuery(id+"F2.imprint","INTERSECT",VERTEX,{"derivedFrom":[subQ0,sQuery(id+"F2.wireOp",EDGE,"E8.right")]}),1.0]])],"derivedFrom":subQ0})])],"isStart":true});}
            var Q6;
            {var subQ0=sQuery(id+"F2.wireOp",EDGE,"E11.0");Q6=makeQuery(id+"F3.opExtrude","CAP_EDGE",EDGE,{"disambiguationData":[OSD([subQ0]),TDD([makeQuery(id+"F2.imprint","IMPRINT",EDGE,{"disambiguationData":[TD([[makeQuery(id+"F2.imprint","INTERSECT",VERTEX,{"disambiguationData":[OD(1.0)],"derivedFrom":[sQuery(id+"F2.wireOp",EDGE,"E8.bottom"),subQ0]}),1.0]])],"derivedFrom":subQ0})])],"isStart":true});}
            var Q7;
            {var subQ0=sQuery(id+"F2.wireOp",EDGE,"E11.0");Q7=makeQuery(id+"F3.opExtrude","CAP_EDGE",EDGE,{"disambiguationData":[OSD([subQ0]),TDD([makeQuery(id+"F2.imprint","IMPRINT",EDGE,{"disambiguationData":[TD([[makeQuery(id+"F2.imprint","INTERSECT",VERTEX,{"disambiguationData":[OD(0.0)],"derivedFrom":[sQuery(id+"F2.wireOp",EDGE,"E8.bottom"),subQ0]}),-1.0]])],"derivedFrom":subQ0})])],"isStart":true});}
            var Q8;
            {var subQ0=sQuery(id+"F2.wireOp",EDGE,"E8.bottom");Q8=makeQuery(id+"F3.opExtrude","CAP_EDGE",EDGE,{"disambiguationData":[OSD([subQ0]),TDD([makeQuery(id+"F2.imprint","IMPRINT",EDGE,{"disambiguationData":[TD([[makeQuery(id+"F2.imprint","INTERSECT",VERTEX,{"derivedFrom":[subQ0,sQuery(id+"F2.wireOp",EDGE,"E8.left")]}),-1.0]])],"derivedFrom":subQ0})])],"isStart":true});}
            var Q9;
            Q9=makeQuery(id+"F3.opExtrude","CAP_EDGE",EDGE,{"disambiguationData":[OSD([sQuery(id+"F2.wireOp",EDGE,"E8.left")])],"isStart":true});
            var Q10;
            Q10=makeQuery(id+"F3.opExtrude","SWEPT_EDGE",EDGE,{"disambiguationData":[OSD([sQuery(id+"F2.wireOp",EDGE,"E8.bottom"),sQuery(id+"F2.wireOp",EDGE,"E8.left")])]});
            var Q11;
            Q11=makeQuery(id+"F3.opExtrude","CAP_EDGE",EDGE,{"disambiguationData":[OSD([sQuery(id+"F2.wireOp",EDGE,"E8.left")])],"isStart":false});
            var Q12;
            {var subQ0=sQuery(id+"F2.wireOp",EDGE,"E8.bottom");Q12=makeQuery(id+"F3.opExtrude","CAP_EDGE",EDGE,{"disambiguationData":[OSD([subQ0]),TDD([makeQuery(id+"F2.imprint","IMPRINT",EDGE,{"disambiguationData":[TD([[makeQuery(id+"F2.imprint","INTERSECT",VERTEX,{"derivedFrom":[subQ0,sQuery(id+"F2.wireOp",EDGE,"E8.left")]}),-1.0]])],"derivedFrom":subQ0})])],"isStart":false});}
            var Q13;
            {var subQ0=sQuery(id+"F2.wireOp",EDGE,"E11.0");Q13=makeQuery(id+"F3.opExtrude","CAP_EDGE",EDGE,{"disambiguationData":[OSD([subQ0]),TDD([makeQuery(id+"F2.imprint","IMPRINT",EDGE,{"disambiguationData":[TD([[makeQuery(id+"F2.imprint","INTERSECT",VERTEX,{"disambiguationData":[OD(0.0)],"derivedFrom":[sQuery(id+"F2.wireOp",EDGE,"E8.bottom"),subQ0]}),-1.0]])],"derivedFrom":subQ0})])],"isStart":false});}
            fillet(context, id + "F9", {"entities" : qUnion([Q0, Q1, Q2, Q3, Q4, Q5, Q6, Q7, Q8, Q9, Q10, Q11, Q12, Q13]), "radius" : 10 * mm, "tangentPropagation" : true, "allowEdgeOverflow" : false});
        }
    });
